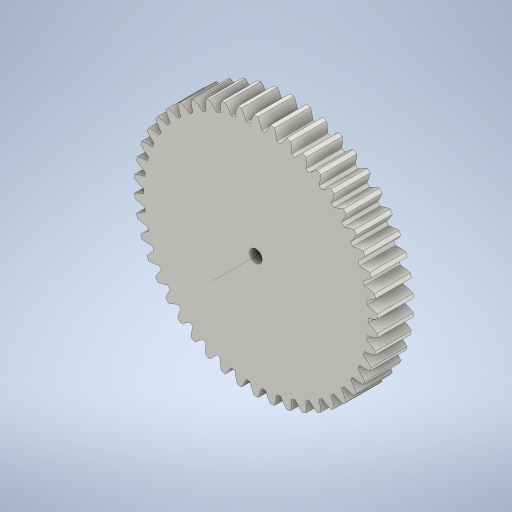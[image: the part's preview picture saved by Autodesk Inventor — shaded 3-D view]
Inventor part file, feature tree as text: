
AUTODESK INVENTOR PART (.ipt)
format: ipt  version: 2023 (Build 270158000, 158)  size: 491,008 bytes
history: native  units: mm (DEFAULTED — no unit token found)
features: other x4, plane x3, sketch x2, extrude x1, hole x1
ambient origin geometry x8: Origin, YZ Plane, XZ Plane, XY Plane, X Axis, Y Axis, Z Axis, Center Point
bodies: Solid1 (feature_tree)
feature tree (11):
  extrude  "Extrusion1"  Depth=10.0mm TaperAngle=0.0deg
  plane  "Work Plane2"
  plane  "Work Plane8"
  plane  "Work Plane9"
  other  "Spur Gear"
  hole  "Hole1"  [1 undecoded]
  other  "Work Axis1"
  sketch  "Sketch1"  dims[d0=67.73172mm d1=10.0mm d2=0.0mm]
  sketch  "Sketch2"  dims[d3=63.25mm d4=10.0mm d5=0.0mm d16=50.0mm d17=0.0mm d34=0.682955mm d39=0.0mm d41=0.0mm d43=50.0mm d46=50.0mm d47=0.0mm d48=0.0mm d58=10.0mm d59=10.0mm d51=3.5mm d52=6.0mm d53=4.0mm d54=2.0mm d55=90.0deg d56=8.0mm d57=20.594885mm]
  other  "Srf1"
  other  "Pitch Diameter"
note: 1 required parameter value undecoded (feature->parameter linkage not recoverable at this tier; creation-order binding heuristic only, values carry confidence <= 0.55)
